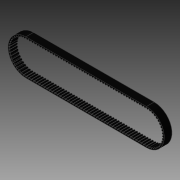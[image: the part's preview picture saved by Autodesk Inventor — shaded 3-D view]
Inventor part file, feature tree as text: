
AUTODESK INVENTOR PART (.ipt)
format: ipt  version: 2014 SP1 (Build 180222100, 222)  size: 1,277,440 bytes
history: native  units: in
note: dims shown in document units (in); Inventor stores cm internally (conversion verified against a paired STEP export)
features: extrude x2, sketch x1, pattern_linear x1
ambient origin geometry x8: Origin, YZ Plane, XZ Plane, XY Plane, X Axis, Y Axis, Z Axis, Center Point
bodies: Solid1 (feature_tree)
feature tree (4):
  sketch  "Sketch1"  dims[d0=1.29in d1=9.2008in d2=1.3315in d3=0.5906in d4=0.0in d6=52.7559in d8=0.0039in d9=0.0681in d10=0.5906in d11=0.0in]
  extrude  "Extrusion1"  Depth=9.2008in
  pattern_linear  "Rectangular Pattern1"  Spacing1=1.3315in  [1 undecoded]
  extrude  "Extrusion2"  Depth=0.5906in TaperAngle=0.0deg
note: 1 required parameter value undecoded (feature->parameter linkage not recoverable at this tier; creation-order binding heuristic only, values carry confidence <= 0.55)
